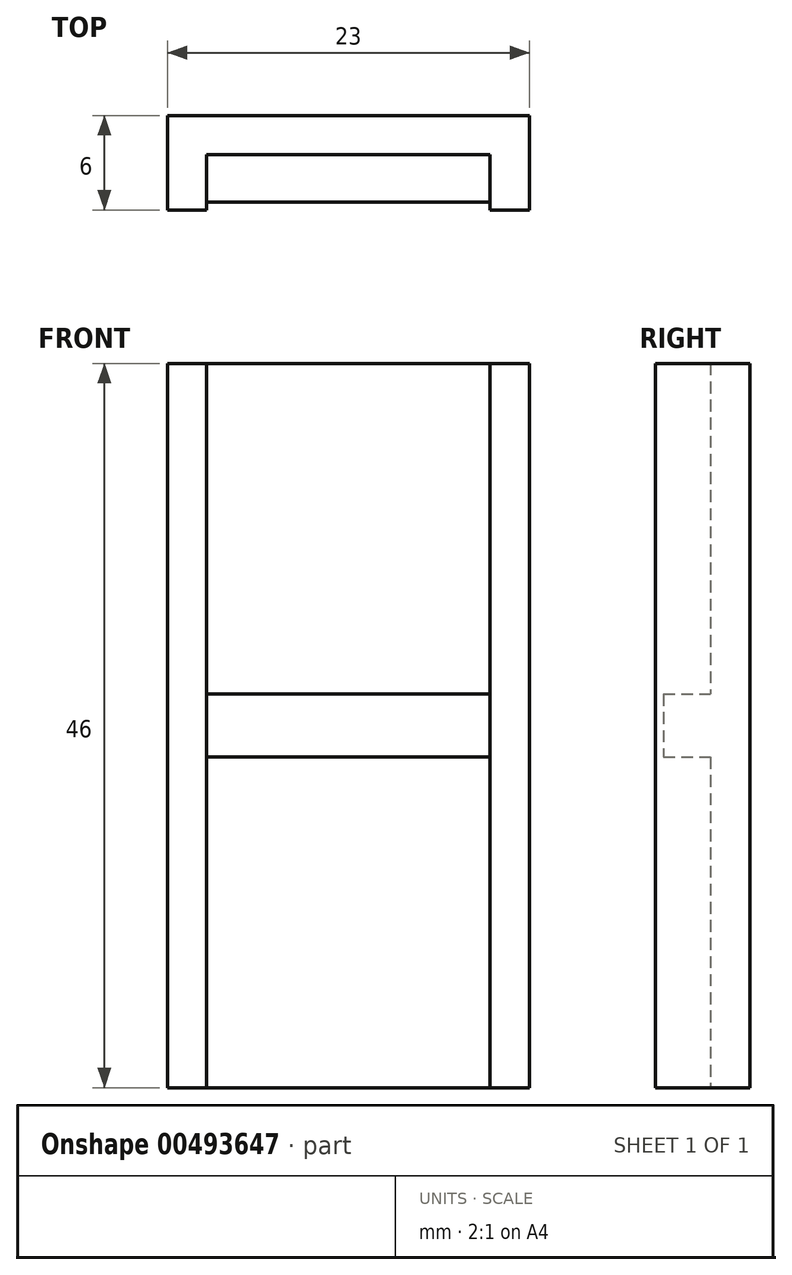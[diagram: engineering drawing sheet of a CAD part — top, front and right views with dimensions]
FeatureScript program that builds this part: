
annotation { "Feature Type Name" : "Feature", "Feature Type Description" : "" }
export const myFeature = defineFeature(function(context is Context, id is Id, definition is map)
    precondition{}
    {
        {
            var Q0;
            Q0=qCreatedBy(makeId("Front.planeOp"),FACE);
            var sketch = newSketch(context, id + "F0", { "sketchPlane" : qUnion([Q0])});
            skLineSegment(sketch, "E0.bottom", {"start": v(-11.5, 30) * mm, "end": v(11.5, 30) * mm});
            skLineSegment(sketch, "E0.top", {"start": v(-11.5, -30) * mm, "end": v(11.5, -30) * mm});
            skLineSegment(sketch, "E0.left", {"start": v(-11.5, 30) * mm, "end": v(-11.5, -30) * mm});
            skLineSegment(sketch, "E0.right", {"start": v(11.5, 30) * mm, "end": v(11.5, -30) * mm});
            skPoint(sketch, "E0.middle", {"position": v(0, 0) * mm});
            skSolve(sketch);
        }
        {
            var Q0;
            Q0=makeQuery(id+"F0.imprint","IMPRINT",FACE,{"disambiguationData":[TD([[makeQuery(id+"F0.imprint","IMPRINT",EDGE,{"derivedFrom":sQuery(id+"F0.wireOp",EDGE,"E0.bottom")}),-1.0]])]});
            extrude(context, id + "F1", {"entities" : qUnion([Q0]), "depth" : 6 * mm});
        }
        {
            var Q0;
            Q0=makeQuery(id+"F1.opExtrude","CAP_FACE",FACE,{"disambiguationData":[OSD([sQuery(id+"F0.wireOp",EDGE,"E0.bottom"),sQuery(id+"F0.wireOp",EDGE,"E0.top"),sQuery(id+"F0.wireOp",EDGE,"E0.left"),sQuery(id+"F0.wireOp",EDGE,"E0.right")])],"isStart":false});
            shell(context, id + "F2", {"entities" : qUnion([Q0]), "thickness" : 2.5 * mm});
        }
        {
            var Q0;
            Q0=makeQuery(id+"F1.opExtrude","SWEPT_FACE",FACE,{"disambiguationData":[OSD([sQuery(id+"F0.wireOp",EDGE,"E0.top")])]});
            var sketch = newSketch(context, id + "F3", { "sketchPlane" : qUnion([Q0])});
            skLineSegment(sketch, "E1.bottom", {"start": v(-11.5, 6) * mm, "end": v(11.5, 6) * mm});
            skLineSegment(sketch, "E1.top", {"start": v(-11.5, 0) * mm, "end": v(11.5, 0) * mm});
            skLineSegment(sketch, "E1.left", {"start": v(-11.5, 6) * mm, "end": v(-11.5, 0) * mm});
            skLineSegment(sketch, "E1.right", {"start": v(11.5, 6) * mm, "end": v(11.5, 0) * mm});
            skSolve(sketch);
        }
        {
            var Q0;
            Q0=makeQuery(id+"F3.imprint","IMPRINT",FACE,{"disambiguationData":[TD([[makeQuery(id+"F3.imprint","IMPRINT",EDGE,{"derivedFrom":sQuery(id+"F3.wireOp",EDGE,"E1.bottom")}),-1.0]])]});
            extrude(context, id + "F4", {"entities" : qUnion([Q0]), "operationType" : NewBodyOperationType.REMOVE, "oppositeDirection" : true, "depth" : 7 * mm});
        }
        {
            var Q0;
            Q0=makeQuery(id+"F1.opExtrude","SWEPT_FACE",FACE,{"disambiguationData":[OSD([sQuery(id+"F0.wireOp",EDGE,"E0.bottom")])]});
            var sketch = newSketch(context, id + "F5", { "sketchPlane" : qUnion([Q0])});
            skLineSegment(sketch, "E2.bottom", {"start": v(-11.5, 0) * mm, "end": v(11.5, 0) * mm});
            skLineSegment(sketch, "E2.top", {"start": v(-11.5, -6) * mm, "end": v(11.5, -6) * mm});
            skLineSegment(sketch, "E2.left", {"start": v(-11.5, 0) * mm, "end": v(-11.5, -6) * mm});
            skLineSegment(sketch, "E2.right", {"start": v(11.5, 0) * mm, "end": v(11.5, -6) * mm});
            skSolve(sketch);
        }
        {
            var Q0;
            Q0=makeQuery(id+"F5.imprint","IMPRINT",FACE,{"disambiguationData":[TD([[makeQuery(id+"F5.imprint","IMPRINT",EDGE,{"derivedFrom":sQuery(id+"F5.wireOp",EDGE,"E2.bottom")}),-1.0]])]});
            extrude(context, id + "F6", {"entities" : qUnion([Q0]), "operationType" : NewBodyOperationType.REMOVE, "oppositeDirection" : true, "depth" : 7 * mm});
        }
        {
            var Q0;
            Q0=makeQuery(id+"F2.opShell","OFFSET_FACE",FACE,{"disambiguationData":[OSD([sQuery(id+"F0.wireOp",EDGE,"E0.bottom"),sQuery(id+"F0.wireOp",EDGE,"E0.top"),sQuery(id+"F0.wireOp",EDGE,"E0.left"),sQuery(id+"F0.wireOp",EDGE,"E0.right")])]});
            var sketch = newSketch(context, id + "F7", { "sketchPlane" : qUnion([Q0])});
            skLineSegment(sketch, "E3.bottom", {"start": v(9, -2) * mm, "end": v(-9, -2) * mm});
            skLineSegment(sketch, "E3.top", {"start": v(9, 2) * mm, "end": v(-9, 2) * mm});
            skLineSegment(sketch, "E3.left", {"start": v(9, -2) * mm, "end": v(9, 2) * mm});
            skLineSegment(sketch, "E3.right", {"start": v(-9, -2) * mm, "end": v(-9, 2) * mm});
            skPoint(sketch, "E3.middle", {"position": v(0, 0) * mm});
            skSolve(sketch);
        }
        {
            var Q0;
            Q0=makeQuery(id+"F7.imprint","IMPRINT",FACE,{"disambiguationData":[TD([[makeQuery(id+"F7.imprint","IMPRINT",EDGE,{"derivedFrom":sQuery(id+"F7.wireOp",EDGE,"E3.bottom")}),-1.0]])]});
            extrude(context, id + "F8", {"entities" : qUnion([Q0]), "operationType" : NewBodyOperationType.ADD, "depth" : 3 * mm});
        }
    });
